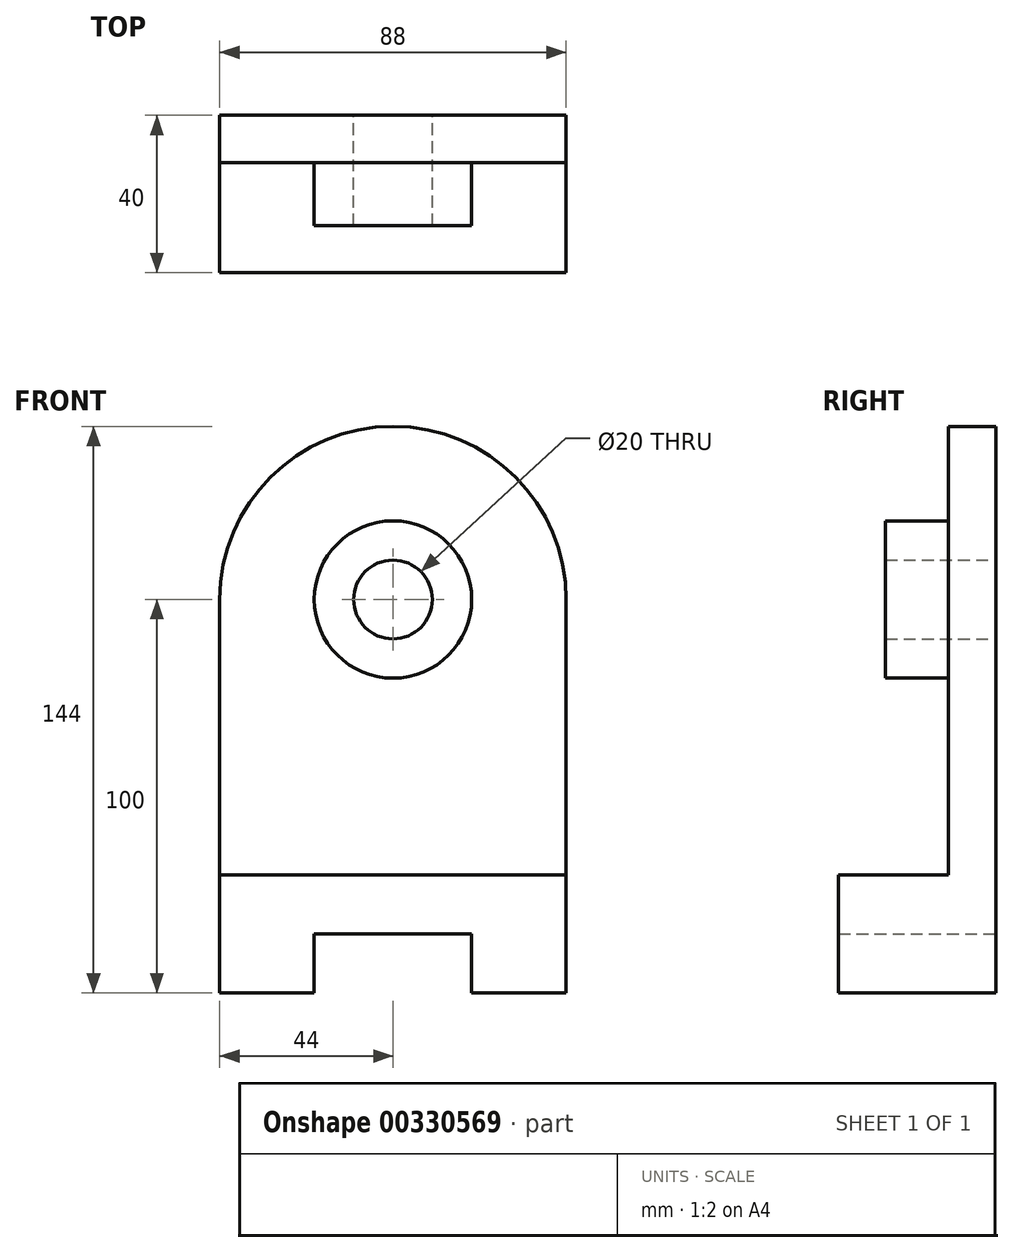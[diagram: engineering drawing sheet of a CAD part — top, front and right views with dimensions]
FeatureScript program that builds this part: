
annotation { "Feature Type Name" : "Feature", "Feature Type Description" : "" }
export const myFeature = defineFeature(function(context is Context, id is Id, definition is map)
    precondition{}
    {
        {
            var Q0;
            Q0=qCreatedBy(makeId("Front.planeOp"),FACE);
            var sketch = newSketch(context, id + "F0", { "sketchPlane" : qUnion([Q0])});
            skLineSegment(sketch, "E0", {"start": v(-44, -68) * mm, "end": v(-20, -68) * mm});
            skLineSegment(sketch, "E1", {"start": v(-20, -68) * mm, "end": v(-20, -53) * mm});
            skLineSegment(sketch, "E2", {"start": v(-20, -53) * mm, "end": v(20, -53) * mm});
            skLineSegment(sketch, "E3", {"start": v(20, -53) * mm, "end": v(20, -68) * mm});
            skLineSegment(sketch, "E4", {"start": v(20, -68) * mm, "end": v(44, -68) * mm});
            skLineSegment(sketch, "E5", {"start": v(44, -68) * mm, "end": v(44, -38) * mm});
            skLineSegment(sketch, "E6", {"start": v(44, -38) * mm, "end": v(-44, -38) * mm});
            skLineSegment(sketch, "E7", {"start": v(-44, -38) * mm, "end": v(-44, -68) * mm});
            skCircle(sketch, "E8", {"center": v(0, 32) * mm, "radius": 10 * mm});
            skCircle(sketch, "E9", {"center": v(0, 32) * mm, "radius": 20 * mm});
            skPoint(sketch, "E10.1.internal.snap0", {"position": v(0, -53) * mm});
            skFitSpline(sketch, "E10", {"points": [v(0, -53) * mm, v(0, -43.11) * mm, v(0, 32) * mm, v(0, 50.37) * mm], "startDerivative": vector(-0.07, 39.2) * mm, "endDerivative": vector(-0.1, 88.85) * mm, "construction": true});
            skFitSpline(sketch, "E11", {"points": [v(0, 32) * mm, v(-65.8, 32) * mm], "startDerivative": vector(-65.48, 0) * mm, "endDerivative": vector(-65.38, 0) * mm, "construction": true});
            skFitSpline(sketch, "E12", {"points": [v(0, 32) * mm, v(54.5, 32) * mm], "startDerivative": vector(54.8, 0) * mm, "endDerivative": vector(54.86, 0) * mm, "construction": true});
            skFitSpline(sketch, "E13", {"points": [v(-44, -38) * mm, v(-44, 32) * mm], "startDerivative": vector(0, 70) * mm, "endDerivative": vector(0, 70) * mm});
            skLineSegment(sketch, "E14", {"start": v(44, -38) * mm, "end": v(44, 32) * mm});
            skArc(sketch, "E15", {"start": v(44, 32) * mm, "mid": v(0, 76) * mm, "end": v(-44, 32) * mm});
            skSolve(sketch);
        }
        {
            var Q0;
            Q0=makeQuery(id+"F0.imprint","IMPRINT",FACE,{"disambiguationData":[TD([[makeQuery(id+"F0.imprint","IMPRINT",EDGE,{"derivedFrom":sQuery(id+"F0.wireOp",EDGE,"E8")}),-1.0]])]});
            extrude(context, id + "F1", {"entities" : qUnion([Q0]), "depth" : 28 * mm});
        }
        {
            var Q0;
            {var subQ0=sQuery(id+"F0.wireOp",EDGE,"E13");Q0=makeQuery(id+"F0.imprint","IMPRINT",FACE,{"disambiguationData":[TD([[makeQuery(id+"F0.imprint","IMPRINT",EDGE,{"derivedFrom":subQ0}),-1.0]])]});}
            var Q1;
            {var subQ5=sQuery(id+"F0.wireOp",EDGE,"E15");Q1=makeQuery(id+"F0.imprint","IMPRINT",FACE,{"disambiguationData":[TD([[makeQuery(id+"F0.imprint","IMPRINT",EDGE,{"derivedFrom":subQ5}),1.0]])]});}
            var Q2;
            {var subQ5=sQuery(id+"F0.wireOp",EDGE,"E14");Q2=makeQuery(id+"F0.imprint","IMPRINT",FACE,{"disambiguationData":[TD([[makeQuery(id+"F0.imprint","IMPRINT",EDGE,{"derivedFrom":subQ5}),1.0]])]});}
            extrude(context, id + "F2", {"entities" : qUnion([Q0, Q1, Q2]), "operationType" : NewBodyOperationType.ADD, "depth" : 12 * mm});
        }
        {
            var Q0;
            Q0=makeQuery(id+"F0.imprint","IMPRINT",FACE,{"disambiguationData":[TD([[makeQuery(id+"F0.imprint","IMPRINT",EDGE,{"derivedFrom":sQuery(id+"F0.wireOp",EDGE,"E0")}),1.0]])]});
            var Q1;
            {var subQ6=sQuery(id+"F0.wireOp",EDGE,"E3");Q1=makeQuery(id+"F0.imprint","IMPRINT",FACE,{"disambiguationData":[TD([[makeQuery(id+"F0.imprint","IMPRINT",EDGE,{"derivedFrom":subQ6}),1.0]])]});}
            extrude(context, id + "F3", {"entities" : qUnion([Q0, Q1]), "operationType" : NewBodyOperationType.ADD, "depth" : 40 * mm});
        }
    });
